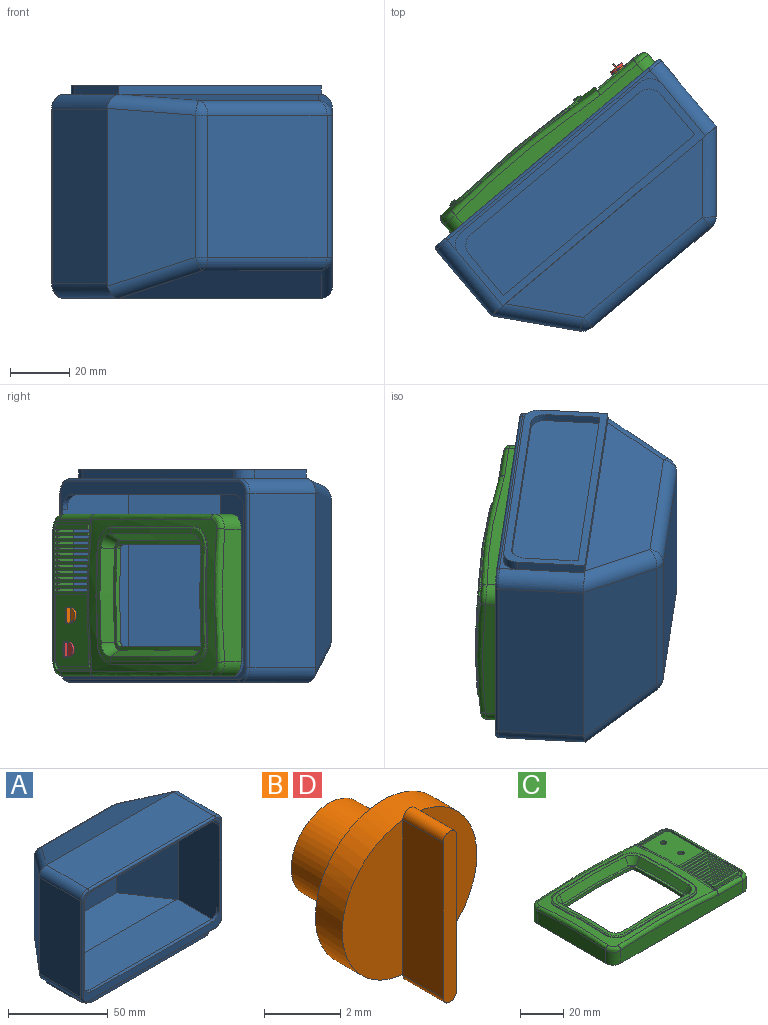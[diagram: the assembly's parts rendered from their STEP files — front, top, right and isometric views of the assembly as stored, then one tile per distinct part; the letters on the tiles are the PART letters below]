
ASSEMBLY  parts=4 mates=3
PART A: 63 faces, bbox 100.4x55x72.5 mm
  f0: plane 89.5x28mm, normal (0,0,-1), area 562.5mm2, adj f2,f30,f31,f33,f47,f48,f49,f50
  f1: plane 97.5x67mm, normal (0,-1,0), area 667mm2, adj f3,f4,f19,f21,f22,f23,f24,f25
  f2: plane 23x3mm, normal (1,0,0), area 69mm2, adj f0,f27,f30,f53
  f3: plane 60x29.27mm, normal (-1,0,0), area 1739.2mm2, adj f1,f16,f18,f20,f23,f25
  f4: plane 60x29.27mm, normal (1,0,0), area 1739.2mm2, adj f1,f14,f18,f20,f22,f24
  f5: plane 89.7x21.95mm, normal (0,0.39,0.92), area 1697mm2, adj f11,f28,f29,f39,f43,f45
  f6: plane 60.24x23.27mm, normal (-0.76,0.64,0), area 1644.2mm2, adj f12,f26,f29,f36,f42,f45
  f7: plane 87.27x20.5mm, normal (0,0.1,-1), area 1442.1mm2, adj f30,f34,f36,f37
  f8: plane 60.24x23.27mm, normal (0.76,0.64,0), area 1644.2mm2, adj f10,f27,f28,f34,f38,f39
  f9: plane 52.73x48.08mm, normal (0,1,0), area 2535.6mm2, adj f37,f38,f42,f43
  f10: plane 59x29mm, normal (1,0,0), area 1711mm2, adj f8,f27,f28,f60
  f11: plane 89.5x29mm, normal (0,0,1), area 2595.5mm2, adj f5,f28,f29,f61
  f12: plane 59x29mm, normal (-1,0,0), area 1711mm2, adj f6,f26,f29,f57
  f13: plane 91.28x23.41mm, normal (0,-0.39,-0.92), area 1903.2mm2, adj f14,f16,f17,f19,f24,f25
  f14: plane 64.08x23.73mm, normal (0.76,-0.64,0), area 1824.6mm2, adj f4,f13,f15,f17,f18,f24
  f15: plane 94.44x23.1mm, normal (0,-0.1,1), area 1740.8mm2, adj f14,f16,f17,f18
  f16: plane 64.08x23.73mm, normal (-0.76,-0.64,0), area 1824.6mm2, adj f3,f13,f15,f17,f18,f25
  f17: plane 55.53x52.79mm, normal (0,-1,0), area 2931mm2, adj f13,f14,f15,f16
  f18: plane 95.5x27.9mm, normal (0,0,1), area 2664.1mm2, adj f3,f4,f14,f15,f16,f20
  f19: plane 85.5x29.59mm, normal (0,0,-1), area 2530.3mm2, adj f1,f13,f24,f25
  f20: plane 95.5x8.5mm, normal (0,1,0), area 345mm2, adj f3,f4,f18,f21,f22,f23
  f21: plane 85.5x2mm, normal (0,0,1), area 171mm2, adj f1,f20,f22,f23
  f22: cylinder r=5mm len=5mm, axis (0,-1,0), area 15.7mm2, adj f1,f4,f20,f21
  f23: cylinder r=5mm len=5mm, axis (0,-1,0), area 15.7mm2, adj f1,f3,f20,f21
  f24: cylinder r=5mm len=31.77mm, axis (0,1,0), area 237.3mm2, adj f1,f4,f13,f14,f19
  f25: cylinder r=5mm len=31.77mm, axis (0,1,0), area 237.3mm2, adj f1,f3,f13,f16,f19
  f26: cylinder r=5mm len=29.04mm, axis (0,-1,0), area 227.8mm2, adj f6,f12,f30,f31,f32,f36,f55
  f27: cylinder r=5mm len=29.04mm, axis (0,-1,0), area 227.8mm2, adj f2,f8,f10,f30,f32,f34,f58
  f28: cylinder r=5mm len=29.36mm, axis (0,-1,0), area 229.4mm2, adj f5,f8,f10,f11,f39,f62
  f29: cylinder r=5mm len=29.36mm, axis (0,-1,0), area 229.4mm2, adj f5,f6,f11,f12,f45,f59
  f30: plane 98.36x5.69mm, normal (0,1,0), area 270mm2, adj f0,f2,f7,f26,f27,f31,f34,f36
  f31: plane 23x3mm, normal (-1,0,0), area 69mm2, adj f0,f26,f30,f54
  f32: plane 89.5x6mm, normal (0,0,-1), area 100.2mm2, adj f26,f27,f33,f53,f54,f56
  f33: plane 79.5x3mm, normal (0,-1,0), area 238.5mm2, adj f0,f32,f53,f54
  f34: cylinder r=5mm len=25.95mm, axis (0.64,-0.76,-0.08), area 220.3mm2, adj f7,f8,f27,f30,f35
  f35: sphere r=5mm, area 19.9mm2, adj f34,f37,f38
  f36: cylinder r=5mm len=25.95mm, axis (-0.64,-0.76,-0.08), area 220.3mm2, adj f6,f7,f26,f30,f40
  f37: cylinder r=5mm len=52.73mm, axis (-1,0,0), area 387.8mm2, adj f7,f9,f35,f40
  f38: cylinder r=5mm len=48.08mm, axis (0,0,1), area 209.4mm2, adj f8,f9,f35,f41
  f39: cylinder r=5mm len=24.62mm, axis (0.61,-0.73,0.31), area 206.3mm2, adj f5,f8,f28,f41
  f40: sphere r=5mm, area 19.9mm2, adj f36,f37,f42
  f41: sphere r=5mm, area 15mm2, adj f38,f39,f43
  f42: cylinder r=5mm len=48.08mm, axis (0,0,1), area 209.4mm2, adj f6,f9,f40,f44
  f43: cylinder r=5mm len=52.73mm, axis (-1,0,0), area 308.7mm2, adj f5,f9,f41,f44
  f44: sphere r=5mm, area 15mm2, adj f42,f43,f45
  f45: cylinder r=5mm len=24.62mm, axis (-0.61,-0.73,0.31), area 206.3mm2, adj f5,f6,f29,f44
  f46: plane 84.5x23mm, normal (0,0,-1), area 1932.8mm2, adj f47,f48,f49,f50,f51,f52
  f47: plane 18x2.5mm, normal (-1,0,0), area 45mm2, adj f0,f46,f48,f51
  f48: plane 84.5x2.5mm, normal (0,-1,0), area 211.3mm2, adj f0,f46,f47,f49
  f49: plane 18x2.5mm, normal (1,0,0), area 45mm2, adj f0,f46,f48,f52
  f50: plane 74.5x2.5mm, normal (0,1,0), area 186.3mm2, adj f0,f46,f51,f52
  f51: cylinder r=5mm len=5mm, axis (0,0,-1), area 19.6mm2, adj f0,f46,f47,f50
  f52: cylinder r=5mm len=5mm, axis (0,0,1), area 19.6mm2, adj f0,f46,f49,f50
  f53: cylinder r=5mm len=5mm, axis (0,0,1), area 23.6mm2, adj f0,f2,f32,f33
  f54: cylinder r=5mm len=5mm, axis (0,0,-1), area 23.6mm2, adj f0,f31,f32,f33
  f55: torus R=4mm, axis (0,-1,0), area 11.4mm2, adj f1,f26,f56,f57
  f56: cylinder r=1mm len=89.5mm, axis (-1,0,0), area 140.6mm2, adj f1,f32,f55,f58
  f57: cylinder r=1mm len=59mm, axis (0,0,-1), area 92.7mm2, adj f1,f12,f55,f59
  f58: torus R=4mm, axis (0,-1,0), area 11.4mm2, adj f1,f27,f56,f60
  f59: torus R=4mm, axis (0,-1,0), area 11.4mm2, adj f1,f29,f57,f61
  f60: cylinder r=1mm len=59mm, axis (0,0,-1), area 92.7mm2, adj f1,f10,f58,f62
  f61: cylinder r=1mm len=89.5mm, axis (1,0,0), area 140.6mm2, adj f1,f11,f59,f62
  f62: torus R=4mm, axis (0,-1,0), area 11.4mm2, adj f1,f28,f60,f61
PART B: 13 faces, bbox 5x4.5x5.5 mm
  f0: plane 4.98x2.25mm, normal (0,-1,0), area 8.6mm2, adj f3,f11
  f1: cylinder r=1.4mm len=2.8mm, axis (0,-1,0), area 17.6mm2, adj f2,f4
  f2: plane 2.8x2.8mm, normal (0,1,0), area 6.2mm2, adj f1
  f3: cylinder r=2.5mm len=5mm, axis (0,-1,0), area 15.7mm2, adj f0,f4,f5,f6,f7
  f4: plane 5x5mm, normal (0,1,0), area 13.5mm2, adj f1,f3
  f5: plane 4.98x2.25mm, normal (0,-1,0), area 8.6mm2, adj f3,f9
  f6: plane 0.5x0.26mm, normal (0,1,0), area 0.1mm2, adj f3,f8,f9,f11
  f7: plane 0.5x0.26mm, normal (0,1,0), area 0.1mm2, adj f3,f9,f10,f11
  f8: cylinder r=0.25mm len=1.5mm, axis (0,1,0), area 1.2mm2, adj f6,f9,f11,f12
  f9: plane 5x1.5mm, normal (-1,0,0), area 7.5mm2, adj f5,f6,f7,f8,f10,f12
  f10: cylinder r=0.25mm len=1.5mm, axis (0,1,0), area 1.2mm2, adj f7,f9,f11,f12
  f11: plane 5x1.5mm, normal (1,0,0), area 7.5mm2, adj f0,f6,f7,f8,f10,f12
  f12: plane 5.5x0.5mm, normal (0,-1,0), area 2.7mm2, adj f8,f9,f10,f11
PART C: 243 faces, bbox 93.4x63x15.4 mm
  f0: cylinder r=5mm len=3.12mm, axis (0,0,-1), area 0.2mm2, adj f28,f36,f57
  f1: plane 1.5x1mm, normal (-1,0,0), area 1.5mm2, adj f182,f212,f213,f214
  f2: plane 1.5x1mm, normal (-1,0,0), area 1.5mm2, adj f182,f206,f207,f208
  f3: plane 1.5x1mm, normal (-1,0,0), area 1.5mm2, adj f182,f209,f210,f211
  f4: plane 1.5x1mm, normal (-1,0,0), area 1.5mm2, adj f182,f185,f186,f187
  f5: plane 1.5x1mm, normal (-1,0,0), area 1.5mm2, adj f182,f188,f189,f190
  f6: plane 1.5x1mm, normal (-1,0,0), area 1.5mm2, adj f182,f191,f192,f193
  f7: plane 1.5x1mm, normal (-1,0,0), area 1.5mm2, adj f182,f194,f195,f196
  f8: plane 1.5x1mm, normal (-1,0,0), area 1.5mm2, adj f182,f197,f198,f199
  f9: plane 1.5x1mm, normal (-1,0,0), area 1.5mm2, adj f182,f200,f201,f202
  f10: plane 1.5x1mm, normal (-1,0,0), area 1.5mm2, adj f182,f203,f204,f205
  f11: plane 25.53x1.5mm, normal (-1,0,0), area 26mm2, adj f25,f178,f182,f215,f216,f217
  f12: plane 51.3x20.96mm, normal (0,0,-1), area 865mm2, adj f121,f136,f137,f138,f139,f140,f183,f185
  f13: plane 1.5x1mm, normal (1,0,0), area 1.5mm2, adj f182,f212,f213,f214
  f14: plane 1.5x1mm, normal (1,0,0), area 1.5mm2, adj f182,f206,f207,f208
  f15: plane 1.5x1mm, normal (1,0,0), area 1.5mm2, adj f182,f209,f210,f211
  f16: plane 1.5x1mm, normal (1,0,0), area 1.5mm2, adj f182,f185,f186,f187
  f17: plane 1.5x1mm, normal (1,0,0), area 1.5mm2, adj f182,f188,f189,f190
  f18: plane 1.5x1mm, normal (1,0,0), area 1.5mm2, adj f182,f191,f192,f193
  f19: plane 1.5x1mm, normal (1,0,0), area 1.5mm2, adj f182,f194,f195,f196
  f20: plane 1.5x1mm, normal (1,0,0), area 1.5mm2, adj f182,f197,f198,f199
  f21: plane 1.5x1mm, normal (1,0,0), area 1.5mm2, adj f182,f200,f201,f202
  f22: plane 1.5x1mm, normal (1,0,0), area 1.5mm2, adj f182,f203,f204,f205
  f23: plane 23.53x1.5mm, normal (1,0,0), area 24mm2, adj f25,f179,f182,f215,f216,f217
  f24: cylinder r=2mm len=1.93mm, axis (0,0,1), area 3.9mm2, adj f180,f182,f183,f184
  f25: plane 24.53x17.41mm, normal (0,0,1), area 412.2mm2, adj f11,f23,f178,f179,f215,f225,f226
  f26: plane 17.76x0.5mm, normal (0,0,1), area 8.2mm2, adj f44,f52,f53,f175
  f27: plane 90x54.9mm, normal (0,0,-1), area 414.8mm2, adj f30,f31,f34,f35,f45,f46,f47,f48
  f28: plane 56x45mm, normal (0,0,-1), area 279.8mm2, adj f0,f36,f37,f38,f39,f40,f41,f42
  f29: bspline ~69.29x60mm, area 751mm2, adj f44,f63,f69,f75,f81,f88,f95,f102
  f30: plane 44.9x6.9mm, normal (1,0,0), area 309.8mm2, adj f27,f45,f46,f51
  f31: plane 44.93x8.81mm, normal (-1,0,0), area 361.8mm2, adj f27,f47,f48,f167
  f32: plane 18.26x0.89mm, normal (0,0,1), area 14.4mm2, adj f44,f49,f50,f171
  f33: plane 30.82x0.68mm, normal (0.99,0,-0.15), area 9.8mm2, adj f44,f181
  f34: plane 81.86x10.37mm, normal (0,1,0), area 620.2mm2, adj f27,f46,f48,f53,f169
  f35: plane 81.86x10.4mm, normal (0,-1,0), area 621.8mm2, adj f27,f45,f47,f49,f165
  f36: plane 32.02x0.7mm, normal (-1,0,0), area 16.1mm2, adj f0,f28,f37,f57,f96,f103
  f37: cylinder r=5mm len=5mm, axis (0,0,-1), area 0.4mm2, adj f28,f36,f38,f96
  f38: plane 43.08x0.87mm, normal (0,1,0), area 23.7mm2, adj f28,f37,f39,f82,f89,f96
  f39: cylinder r=5mm len=5mm, axis (0,0,-1), area 0.6mm2, adj f28,f38,f40,f82
  f40: plane 32.03x0.73mm, normal (1,0,0), area 16.7mm2, adj f28,f39,f41,f54,f56,f82
  f41: cylinder r=5mm len=5mm, axis (0,0,-1), area 0.4mm2, adj f28,f40,f42,f56
  f42: plane 43.08x0.85mm, normal (0,-1,0), area 22.8mm2, adj f28,f41,f43,f55,f56,f57
  f43: cylinder r=5mm len=2.02mm, axis (0,0,-1), area 0.1mm2, adj f28,f42,f57
  f44: bspline ~55.3x3.38mm, area 94.5mm2, adj f26,f29,f32,f33,f49,f53,f165,f169
  f45: cylinder r=5mm len=6.9mm, axis (0,0,-1), area 54.2mm2, adj f27,f30,f35,f50
  f46: cylinder r=5mm len=6.9mm, axis (0,0,-1), area 54.2mm2, adj f27,f30,f34,f52
  f47: cylinder r=5mm len=7.39mm, axis (0,0,1), area 57.7mm2, adj f27,f31,f35,f166
  f48: cylinder r=5mm len=7.37mm, axis (0,0,1), area 57.5mm2, adj f27,f31,f34,f168
  f49: cylinder r=1.8mm len=16.28mm, axis (1,0,0), area 45.6mm2, adj f32,f35,f44,f50
  f50: torus R=3.2mm, axis (0,0,1), area 19.3mm2, adj f32,f45,f49,f51,f172
  f51: cylinder r=1.8mm len=44.9mm, axis (0,-1,0), area 127mm2, adj f30,f50,f52,f173
  f52: torus R=3.2mm, axis (0,0,1), area 19.3mm2, adj f26,f46,f51,f53,f174
  f53: cylinder r=1.8mm len=16.28mm, axis (1,0,0), area 45.6mm2, adj f26,f34,f44,f52
  f54: bspline ~31.66x6mm, area 115.8mm2, adj f40,f56,f76,f82
  f55: bspline ~42.85x6mm, area 159.8mm2, adj f42,f56,f57,f64
  f56: bspline ~7.72x7.57mm, area 20.3mm2, adj f40,f41,f42,f54,f55,f70
  f57: bspline ~7.6x7.56mm, area 20.3mm2, adj f0,f28,f36,f42,f43,f55,f58,f103
  f58: bspline ~1.75x1.6mm, area 4.1mm2, adj f57,f59,f64,f104
  f59: bspline ~2.76x2.74mm, area 4.2mm2, adj f58,f60,f65,f105
  f60: bspline ~5.09x5.02mm, area 27.3mm2, adj f59,f61,f66,f106
  f61: bspline ~6.51x6.5mm, area 15.6mm2, adj f60,f62,f67,f107
  f62: bspline ~7.29x7.29mm, area 9.3mm2, adj f61,f63,f68,f108
  f63: bspline ~7.64x7.6mm, area 5.1mm2, adj f29,f62,f69,f109
  f64: bspline ~42.62x2.37mm, area 72.4mm2, adj f55,f58,f65,f70
  f65: bspline ~42.62x1.26mm, area 53.7mm2, adj f59,f64,f66,f71
  f66: bspline ~43.08x4.72mm, area 198.8mm2, adj f60,f65,f67,f72
  f67: bspline ~43.08x1.76mm, area 75.9mm2, adj f61,f66,f68,f73
  f68: bspline ~43.07x1.07mm, area 36.8mm2, adj f62,f67,f69,f74
  f69: bspline ~43.03x1.13mm, area 19.5mm2, adj f29,f63,f68,f75
  f70: bspline ~1.75x1.59mm, area 4.1mm2, adj f56,f64,f71,f76
  f71: bspline ~2.75x2.74mm, area 4.2mm2, adj f65,f70,f72,f77
  f72: bspline ~5.06x5.01mm, area 27.3mm2, adj f66,f71,f73,f78
  f73: bspline ~6.51x6.5mm, area 15.6mm2, adj f67,f72,f74,f79
  f74: bspline ~7.29x7.29mm, area 9.3mm2, adj f68,f73,f75,f80
  f75: bspline ~7.64x7.6mm, area 5.1mm2, adj f29,f69,f74,f81
  f76: bspline ~31.56x2.39mm, area 53.6mm2, adj f54,f70,f77,f83
  f77: bspline ~31.56x1.26mm, area 39.8mm2, adj f71,f76,f78,f84
  f78: bspline ~32.41x5.57mm, area 147.7mm2, adj f72,f77,f79,f85
  f79: bspline ~32.08x1.76mm, area 56.5mm2, adj f73,f78,f80,f86
  f80: bspline ~32.08x0.89mm, area 27.4mm2, adj f74,f79,f81,f87
  f81: bspline ~32.04x6.09mm, area 13.9mm2, adj f29,f75,f80,f88
  f82: bspline ~7.68x7.6mm, area 20.2mm2, adj f38,f39,f40,f54,f83,f89
  f83: bspline ~1.75x1.59mm, area 4.1mm2, adj f76,f82,f84,f90
  f84: bspline ~2.76x2.74mm, area 4.2mm2, adj f77,f83,f85,f91
  f85: bspline ~5.09x5.01mm, area 27.3mm2, adj f78,f84,f86,f92
  f86: bspline ~6.51x6.5mm, area 15.6mm2, adj f79,f85,f87,f93
  f87: bspline ~7.29x7.29mm, area 9.3mm2, adj f80,f86,f88,f94
  f88: bspline ~7.75x7.6mm, area 5.1mm2, adj f29,f81,f87,f95
  f89: bspline ~42.85x6mm, area 159.6mm2, adj f38,f82,f90,f96
  f90: bspline ~42.62x2.38mm, area 72.4mm2, adj f83,f89,f91,f97
  f91: bspline ~42.62x1.26mm, area 53.7mm2, adj f84,f90,f92,f98
  f92: bspline ~43.51x4.73mm, area 198.8mm2, adj f85,f91,f93,f99
  f93: bspline ~43.08x1.76mm, area 75.9mm2, adj f86,f92,f94,f100
  f94: bspline ~43.07x1.07mm, area 36.8mm2, adj f87,f93,f95,f101
  f95: bspline ~43.03x1.13mm, area 19.5mm2, adj f29,f88,f94,f102
  f96: bspline ~7.69x7.6mm, area 20.3mm2, adj f36,f37,f38,f89,f97,f103
  f97: bspline ~1.75x1.59mm, area 4.1mm2, adj f90,f96,f98,f104
  f98: bspline ~2.76x2.74mm, area 4.2mm2, adj f91,f97,f99,f105
  f99: bspline ~5.01x5.01mm, area 27.3mm2, adj f92,f98,f100,f106
  f100: bspline ~6.51x6.5mm, area 15.6mm2, adj f93,f99,f101,f107
  f101: bspline ~7.29x7.29mm, area 9.3mm2, adj f94,f100,f102,f108
  f102: bspline ~7.76x7.6mm, area 5.1mm2, adj f29,f95,f101,f109
  f103: bspline ~31.34x6.02mm, area 115.9mm2, adj f36,f57,f96,f104
  f104: bspline ~31.56x2.22mm, area 53.6mm2, adj f58,f97,f103,f105
  f105: bspline ~31.56x1.28mm, area 39.8mm2, adj f59,f98,f104,f106
  f106: bspline ~32.08x5.37mm, area 147.7mm2, adj f60,f99,f105,f107
  f107: bspline ~32.41x1.76mm, area 56.5mm2, adj f61,f100,f106,f108
  f108: bspline ~32.08x0.9mm, area 27.4mm2, adj f62,f101,f107,f109
  f109: bspline ~32.04x0.95mm, area 13.8mm2, adj f29,f63,f102,f108
  f110: offset ~35.41x8.43mm, area 100.3mm2, adj f111,f112,f162,f163
  f111: offset ~8.1x8.02mm, area 25mm2, adj f110,f117,f144,f145,f162
  f112: offset ~8.06x8.05mm, area 25mm2, adj f110,f113,f156,f159,f160
  f113: offset ~46.51x8.55mm, area 135.2mm2, adj f112,f114,f153,f156,f157
  f114: offset ~7.54x7.52mm, area 25mm2, adj f113,f115,f141,f153,f154
  f115: offset ~34.98x6.29mm, area 100.3mm2, adj f114,f116,f141,f143,f151
  f116: offset ~8.06x8.05mm, area 25mm2, adj f115,f117,f142,f143,f149
  f117: offset ~45.99x6.43mm, area 135.2mm2, adj f111,f116,f142,f144,f147
  f118: offset ~72.29x63mm, area 1103.2mm2, adj f120,f121,f122,f123,f134,f135,f146,f148
  f119: plane 44.9x6.9mm, normal (-1,0,0), area 309.8mm2, adj f27,f132,f133,f138
  f120: plane 44.93x8.91mm, normal (1,0,0), area 382.7mm2, adj f27,f118,f134,f135
  f121: plane 51.92x1.99mm, normal (-0.99,0,0.15), area 63.4mm2, adj f12,f118,f122,f123,f136,f140
  f122: plane 81.97x10.88mm, normal (0,-1,0), area 648.1mm2, adj f27,f118,f121,f133,f135,f140
  f123: plane 81.97x10.91mm, normal (0,1,0), area 649.7mm2, adj f27,f118,f121,f132,f134,f136
  f124: plane 32x2.18mm, normal (1,0,0), area 64.1mm2, adj f28,f125,f131,f144,f159,f162
  f125: cylinder r=6.5mm len=6.5mm, axis (0,0,-1), area 16.6mm2, adj f28,f124,f126,f159
  f126: plane 43x2.27mm, normal (0,-1,0), area 87.4mm2, adj f28,f125,f127,f153,f156,f159
  f127: cylinder r=6.5mm len=6.5mm, axis (0,0,-1), area 16.8mm2, adj f28,f126,f128,f153
  f128: plane 32x2.2mm, normal (-1,0,0), area 64.8mm2, adj f28,f127,f129,f141,f143,f153
  f129: cylinder r=6.5mm len=6.5mm, axis (0,0,-1), area 16.6mm2, adj f28,f128,f130,f143
  f130: plane 43x2.25mm, normal (0,1,0), area 86.4mm2, adj f28,f129,f131,f142,f143,f144
  f131: cylinder r=6.5mm len=6.5mm, axis (0,0,-1), area 16.4mm2, adj f28,f124,f130,f144
  f132: cylinder r=3.5mm len=6.9mm, axis (0,0,-1), area 37.9mm2, adj f27,f119,f123,f137
  f133: cylinder r=3.5mm len=6.9mm, axis (0,0,-1), area 37.9mm2, adj f27,f119,f122,f139
  f134: cylinder r=3.5mm len=7.86mm, axis (0,0,1), area 42.9mm2, adj f27,f118,f120,f123
  f135: cylinder r=3.5mm len=7.83mm, axis (0,0,1), area 42.8mm2, adj f27,f118,f120,f122
  f136: cylinder r=0.3mm len=17.8mm, axis (1,0,0), area 8.4mm2, adj f12,f121,f123,f137
  f137: torus R=3.2mm, axis (0,0,1), area 2.5mm2, adj f12,f132,f136,f138
  f138: cylinder r=0.3mm len=44.9mm, axis (0,-1,0), area 21.2mm2, adj f12,f119,f137,f139
  f139: torus R=3.2mm, axis (0,0,1), area 2.5mm2, adj f12,f133,f138,f140
  f140: cylinder r=0.3mm len=17.8mm, axis (1,0,0), area 8.4mm2, adj f12,f121,f122,f139
  f141: offset ~34.66x9mm, area 73.8mm2, adj f114,f115,f128,f143,f153
  f142: offset ~45.85x9mm, area 101.8mm2, adj f116,f117,f130,f143,f144
  f143: offset ~10.64x10.57mm, area 20.6mm2, adj f115,f116,f128,f129,f130,f141,f142
  f144: offset ~9.85x9.81mm, area 20.6mm2, adj f111,f117,f124,f130,f131,f142,f162
  f145: offset ~9.51x9.5mm, area 1.3mm2, adj f111,f146,f147,f163,f164
  f146: offset ~10.64x10.6mm, area 6.6mm2, adj f118,f145,f147,f148,f164
  f147: offset ~46.07x3.68mm, area 5.8mm2, adj f117,f145,f146,f148,f149
  f148: offset ~45.9x4.4mm, area 30.9mm2, adj f118,f146,f147,f149,f150
  f149: offset ~8.78x8.77mm, area 1.3mm2, adj f116,f147,f148,f150,f151
  f150: offset ~10.4x10.4mm, area 6.6mm2, adj f118,f148,f149,f151,f152
  f151: offset ~35.08x3.52mm, area 4.3mm2, adj f115,f149,f150,f152,f154
  f152: offset ~35.36x9.11mm, area 22.8mm2, adj f118,f150,f151,f154,f155
  f153: offset ~10.6x10.6mm, area 20.6mm2, adj f113,f114,f126,f127,f128,f141,f156
  f154: offset ~9.51x9.5mm, area 1.3mm2, adj f114,f151,f152,f155,f157
  f155: offset ~10.67x10.6mm, area 6.6mm2, adj f118,f152,f154,f157,f158
  f156: offset ~45.85x9mm, area 101.6mm2, adj f112,f113,f126,f153,f159
  f157: offset ~46.07x3.68mm, area 5.8mm2, adj f113,f154,f155,f158,f160
  f158: offset ~45.9x4.4mm, area 30.9mm2, adj f118,f155,f157,f160,f161
  f159: offset ~10.69x10.64mm, area 20.6mm2, adj f112,f124,f125,f126,f156,f162
  f160: offset ~9.61x9.5mm, area 1.3mm2, adj f112,f157,f158,f161,f163
  f161: offset ~10.76x10.64mm, area 6.6mm2, adj f118,f158,f160,f164
  f162: offset ~34.66x9.02mm, area 73.8mm2, adj f110,f111,f124,f144,f159
  f163: offset ~35.08x3.52mm, area 4.3mm2, adj f110,f145,f160,f164
  f164: offset ~35.36x8.92mm, area 22.7mm2, adj f118,f145,f146,f161,f163
  f165: bspline ~64x3.5mm, area 191.4mm2, adj f29,f35,f44,f166
  f166: bspline ~5x5mm, area 20.1mm2, adj f29,f47,f165,f167
  f167: bspline ~45.26x3.37mm, area 139.3mm2, adj f29,f31,f166,f168
  f168: bspline ~5x5mm, area 20.1mm2, adj f29,f48,f167,f169
  f169: bspline ~67.18x3.87mm, area 191.3mm2, adj f29,f34,f44,f168
  f170: extruded ~9.3x1mm, area 9.1mm2, adj f44,f171,f181,f182
  f171: plane 18.18x1mm, normal (0,1,0), area 18.2mm2, adj f32,f170,f172,f182
  f172: cylinder r=3.2mm len=2.38mm, axis (0,0,1), area 2.7mm2, adj f50,f171,f173,f182
  f173: plane 44.9x1mm, normal (-1,0,0), area 44.9mm2, adj f51,f172,f174,f182
  f174: cylinder r=3.2mm len=2.73mm, axis (0,0,1), area 3.3mm2, adj f52,f173,f175,f182
  f175: plane 17.73x1mm, normal (0,-1,0), area 17.7mm2, adj f26,f174,f176,f182
  f176: extruded ~9.91x1mm, area 10.3mm2, adj f44,f175,f181,f182
  f177: plane 1.5x1.47mm, normal (-1,0,0), area 2.2mm2, adj f180,f182,f183,f184
  f178: plane 15.41x1mm, normal (0,1,0), area 15.4mm2, adj f11,f25,f179,f182
  f179: cylinder r=2mm len=2mm, axis (0,0,1), area 3.1mm2, adj f23,f25,f178,f182
  f180: plane 15.41x1.5mm, normal (0,-1,0), area 23.1mm2, adj f24,f177,f182,f184
  f181: plane 30.79x1mm, normal (1,0,0), area 30.8mm2, adj f33,f170,f176,f182
  f182: plane 50x19.25mm, normal (0,0,1), area 124.9mm2, adj f1,f2,f3,f4,f5,f6,f7,f8
  f183: plane 17.34x2mm, normal (0,1,0), area 34.7mm2, adj f12,f24,f177,f184,f218,f220
  f184: plane 17.34x1.47mm, normal (0,0,1), area 24.8mm2, adj f24,f177,f180,f183
  f185: plane 17.41x2mm, normal (0,1,0), area 34.8mm2, adj f4,f12,f16,f187,f237,f238
  f186: plane 17.41x2mm, normal (0,-1,0), area 34.8mm2, adj f4,f12,f16,f187,f235,f236
  f187: plane 17.41x1mm, normal (0,0,1), area 17.4mm2, adj f4,f16,f185,f186
  f188: plane 17.41x2mm, normal (0,1,0), area 34.8mm2, adj f5,f12,f17,f190,f235,f236
  f189: plane 17.41x2mm, normal (0,-1,0), area 34.8mm2, adj f5,f12,f17,f190,f233,f234
  f190: plane 17.41x1mm, normal (0,0,1), area 17.4mm2, adj f5,f17,f188,f189
  f191: plane 17.41x2mm, normal (0,1,0), area 34.8mm2, adj f6,f12,f18,f193,f233,f234
  f192: plane 17.41x2mm, normal (0,-1,0), area 34.8mm2, adj f6,f12,f18,f193,f231,f232
  f193: plane 17.41x1mm, normal (0,0,1), area 17.4mm2, adj f6,f18,f191,f192
  f194: plane 17.41x2mm, normal (0,1,0), area 34.8mm2, adj f7,f12,f19,f196,f231,f232
  f195: plane 17.41x2mm, normal (0,-1,0), area 34.8mm2, adj f7,f12,f19,f196,f229,f230
  f196: plane 17.41x1mm, normal (0,0,1), area 17.4mm2, adj f7,f19,f194,f195
  f197: plane 17.41x2mm, normal (0,1,0), area 34.8mm2, adj f8,f12,f20,f199,f229,f230
  f198: plane 17.41x2mm, normal (0,-1,0), area 34.8mm2, adj f8,f12,f20,f199,f227,f228
  f199: plane 17.41x1mm, normal (0,0,1), area 17.4mm2, adj f8,f20,f197,f198
  f200: plane 17.41x2mm, normal (0,1,0), area 34.8mm2, adj f9,f12,f21,f202,f227,f228
  f201: plane 17.41x2mm, normal (0,-1,0), area 34.8mm2, adj f9,f12,f21,f202,f223,f224
  f202: plane 17.41x1mm, normal (0,0,1), area 17.4mm2, adj f9,f21,f200,f201
  f203: plane 17.41x2mm, normal (0,1,0), area 34.8mm2, adj f10,f12,f22,f205,f223,f224
  f204: plane 17.41x2mm, normal (0,-1,0), area 34.8mm2, adj f10,f12,f22,f205,f218,f219
  f205: plane 17.41x1mm, normal (0,0,1), area 17.4mm2, adj f10,f22,f203,f204
  f206: plane 17.41x2mm, normal (0,1,0), area 34.8mm2, adj f2,f12,f14,f208,f241,f242
  f207: plane 17.41x2mm, normal (0,-1,0), area 34.8mm2, adj f2,f12,f14,f208,f239,f240
  f208: plane 17.41x1mm, normal (0,0,1), area 17.4mm2, adj f2,f14,f206,f207
  f209: plane 17.41x2mm, normal (0,1,0), area 34.8mm2, adj f3,f12,f15,f211,f239,f240
  f210: plane 17.41x2mm, normal (0,-1,0), area 34.8mm2, adj f3,f12,f15,f211,f237,f238
  f211: plane 17.41x1mm, normal (0,0,1), area 17.4mm2, adj f3,f15,f209,f210
  f212: plane 17.41x2mm, normal (0,1,0), area 34.8mm2, adj f1,f12,f13,f214,f221,f222
  f213: plane 17.41x2mm, normal (0,-1,0), area 34.8mm2, adj f1,f12,f13,f214,f241,f242
  f214: plane 17.41x1mm, normal (0,0,1), area 17.4mm2, adj f1,f13,f212,f213
  f215: plane 17.41x0.5mm, normal (0,1,0), area 8.7mm2, adj f11,f23,f25,f217
  f216: plane 17.41x2mm, normal (0,-1,0), area 34.8mm2, adj f11,f12,f23,f217,f221,f222
  f217: plane 17.41x1mm, normal (0,0,1), area 17.4mm2, adj f11,f23,f215,f216
  f218: plane 1x0.5mm, normal (1,0,0), area 0.5mm2, adj f12,f182,f183,f204
  f219: plane 0.5x0.47mm, normal (-1,0,0), area 0.2mm2, adj f12,f182,f204,f220
  f220: cylinder r=2mm len=0.53mm, axis (0,0,1), area 0.3mm2, adj f12,f182,f183,f219
  f221: plane 1x0.5mm, normal (1,0,0), area 0.5mm2, adj f12,f182,f212,f216
  f222: plane 1x0.5mm, normal (-1,0,0), area 0.5mm2, adj f12,f182,f212,f216
  f223: plane 1x0.5mm, normal (-1,0,0), area 0.5mm2, adj f12,f182,f201,f203
  f224: plane 1x0.5mm, normal (1,0,0), area 0.5mm2, adj f12,f182,f201,f203
  f225: cylinder r=1.5mm len=3mm, axis (0,0,1), area 14.1mm2, adj f12,f25
  f226: cylinder r=1.5mm len=3mm, axis (0,0,1), area 14.1mm2, adj f12,f25
  f227: plane 1x0.5mm, normal (1,0,0), area 0.5mm2, adj f12,f182,f198,f200
  f228: plane 1x0.5mm, normal (-1,0,0), area 0.5mm2, adj f12,f182,f198,f200
  f229: plane 1x0.5mm, normal (1,0,0), area 0.5mm2, adj f12,f182,f195,f197
  f230: plane 1x0.5mm, normal (-1,0,0), area 0.5mm2, adj f12,f182,f195,f197
  f231: plane 1x0.5mm, normal (1,0,0), area 0.5mm2, adj f12,f182,f192,f194
  f232: plane 1x0.5mm, normal (-1,0,0), area 0.5mm2, adj f12,f182,f192,f194
  f233: plane 1x0.5mm, normal (1,0,0), area 0.5mm2, adj f12,f182,f189,f191
  f234: plane 1x0.5mm, normal (-1,0,0), area 0.5mm2, adj f12,f182,f189,f191
  f235: plane 1x0.5mm, normal (1,0,0), area 0.5mm2, adj f12,f182,f186,f188
  f236: plane 1x0.5mm, normal (-1,0,0), area 0.5mm2, adj f12,f182,f186,f188
  f237: plane 1x0.5mm, normal (1,0,0), area 0.5mm2, adj f12,f182,f185,f210
  f238: plane 1x0.5mm, normal (-1,0,0), area 0.5mm2, adj f12,f182,f185,f210
  f239: plane 1x0.5mm, normal (1,0,0), area 0.5mm2, adj f12,f182,f207,f209
  f240: plane 1x0.5mm, normal (-1,0,0), area 0.5mm2, adj f12,f182,f207,f209
  f241: plane 1x0.5mm, normal (1,0,0), area 0.5mm2, adj f12,f182,f206,f213
  f242: plane 1x0.5mm, normal (-1,0,0), area 0.5mm2, adj f12,f182,f206,f213
PART D: same geometry as B
PLACE A rot(axis=(-0.94,-0.34,0),180deg) t=(42.81,-126.72,29.21)mm
PLACE B rot(axis=(0,0,-1),140deg) t=(60.68,-64.41,15.93)mm
PLACE C rot(axis=(-0.89,-0.32,0.32),96.7deg) t=(6.6,-122.45,22.72)mm
PLACE D rot(axis=(0,0,-1),140deg) t=(60.03,-63.64,4.36)mm
MATE revolute C.f225 <-> B.f1  axis (-0.64,0.77,0) through (61.32,-65.18,15.93)mm
MATE revolute C.f226 <-> D.f1  axis (-0.64,0.77,0) through (61.32,-65.18,4.36)mm
MATE fastened C.f46 <-> A.f25  axis (0.64,-0.77,0) through (69.5,-65.17,0.22)mm
